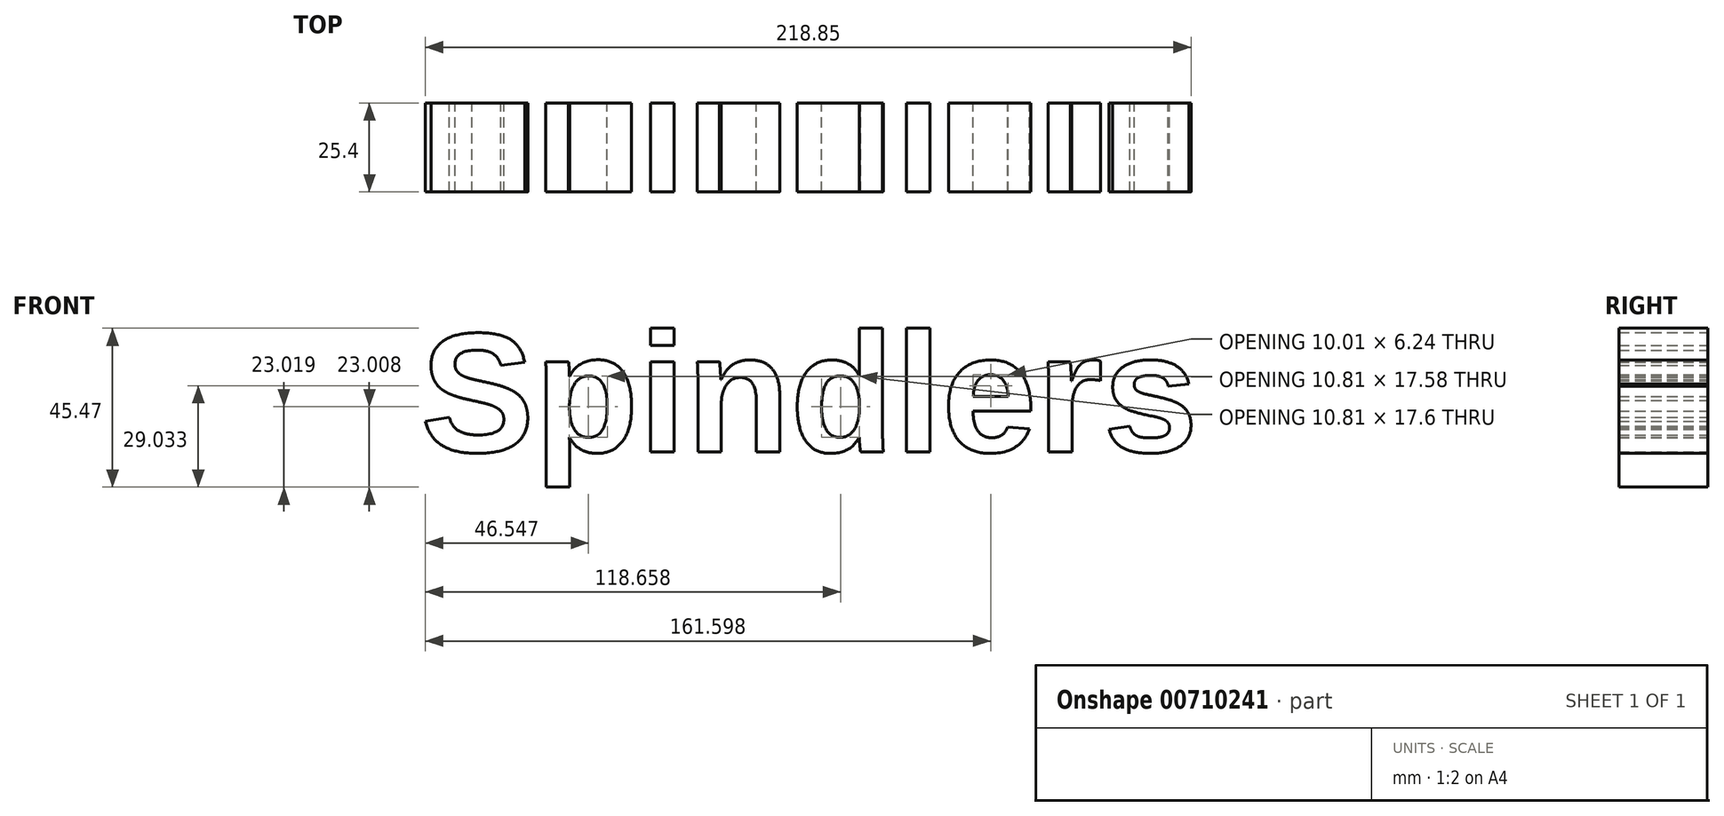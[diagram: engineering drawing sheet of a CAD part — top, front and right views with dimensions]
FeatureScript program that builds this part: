
annotation { "Feature Type Name" : "Feature", "Feature Type Description" : "" }
export const myFeature = defineFeature(function(context is Context, id is Id, definition is map)
    precondition{}
    {
        {
            var Q0;
            Q0=qCreatedBy(makeId("Front.planeOp"),FACE);
            var sketch = newSketch(context, id + "F0", { "sketchPlane" : qUnion([Q0])});
            skText(sketch, "E0", { "text": "Spindlers ", "fontName": "Arimo-Bold.ttf"});
            const initialGuessF0  = {"E0": [-0.05325, -0.0197, 1, 0, 0.03512]};
            skSetInitialGuess(sketch, initialGuessF0);
            skSolve(sketch);
        }
        {
            var Q0;
            Q0 = qSketchRegion(id + "F0", true);
            extrude(context, id + "F1", {"entities" : qUnion([Q0]), "depth" : 25.4 * mm, "offsetDistance" : 25.4 * mm});
        }
    });
